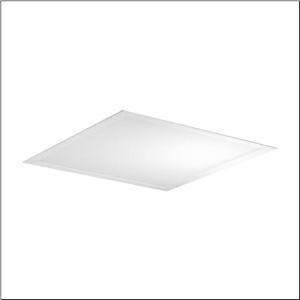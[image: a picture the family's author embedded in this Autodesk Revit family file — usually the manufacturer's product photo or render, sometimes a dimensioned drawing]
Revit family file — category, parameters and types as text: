
# Revit family: apollon_r__21_square_51mq11w72314_ea86
name_source: partatom
category: Lighting Fixtures
units: mm (PartAtom-declared; Revit-internal decimal feet)

## family parameters
Cut with Voids When Loaded = No
Host = Face
Light Source = No
Part Type = Normal
Room Calculation Point = No
Round Connector Dimension = Use Diameter
Shared = No

## types (1)
- Apollon® 21 square (1 x LED, 4100 lm, 23.3 W, 3000K)
    Apparent Load = 23 VA
    CIE Flux Codes = 60 87 97 100 100
    Color Rendering = 80
    Color Temperature = 3000K
    Default Elevation = 1800 mm
    Description = Apollon® 21 square, office luminaire, primary optical cover: micro prismatic cover, of PMMA, CAT 2 (L<= 3000cd/m²), light emission: direct distribution, primary light characteristic: symmetric, installation type: lay-in mounting, LED, rated luminous flux: 4.100lm, luminous efficacy: 176lm/W, light colour: 830, colour temperature: 3000K, with terminal, 3-pole, mains connection: 220..240V, AC/DC, 0/50..60Hz, rated input power: 23.3W, housing, of aluminium, coated, traffic white (RAL 9016), module: M625, length: 620mm, width: 620mm, height: 30mm, housing upper side, of sheet steel, galvanised, protection rating (complete): IP20, protection rating (lamp compartment, on room side): IP50, insulation class (complete): insulation class II (safety insulation), certification: CE, ENEC, impact resistance: IK03, permissible operating ambient temperature: -20..+45°C, permissible storage temperature: -40..+80°C, packaging unit: 1 piece
    Height = 0 mm  [stored 0 ft]
    Lamp = 1 x LED
    Lamp Light Flux = 4100 lm
    Lamp Power = 23.3 W
    Lamp count = 1
    Length = 620 mm
    Luminous efficacy = 176 lm/W
    Manufacturer = Siteco
    ModVariant = No
    Model = 51MQ11W72314
    Mounting Place = Ceiling
    Mounting Type = Recessed
    Number of Poles = 1
    OnlyDefault = Yes
    Power Factor = 1
    Product Name = Apollon® 21 square
    Product group = office luminaire | ceiling recessed
    ProductGroupID = 401
    Protection Class = Protection class II
    Protection Degree = IP 20
    RLX_Detail_Level = 1
    RLX_Emergency_Light_Flux = 0 lm
    RLX_Emergency_Type = 0
    RLX_Emergency_Type_DB = No
    RlxData = <blob elided: 12949 chars, md5=e765a980>
    Socket = socket
    Standby Power = 0 W
    System Light Flux = 4100 lm
    System Power = 23 W
    Type Comments = Product without accessories
    Type Image = l_1291054.jpg
    URL = http://relux.com
    VarID = ---
    Voltage = 0 V
    Weight = 0.00 kg
    Width = 620 mm

note: [stored X ft] marks values corroborated as IEEE doubles in the binary element streams (Revit-internal decimal feet)

## geometry (parser evidence)
native form markers: Sweep x11
no freeform markers — native parametric forms only
